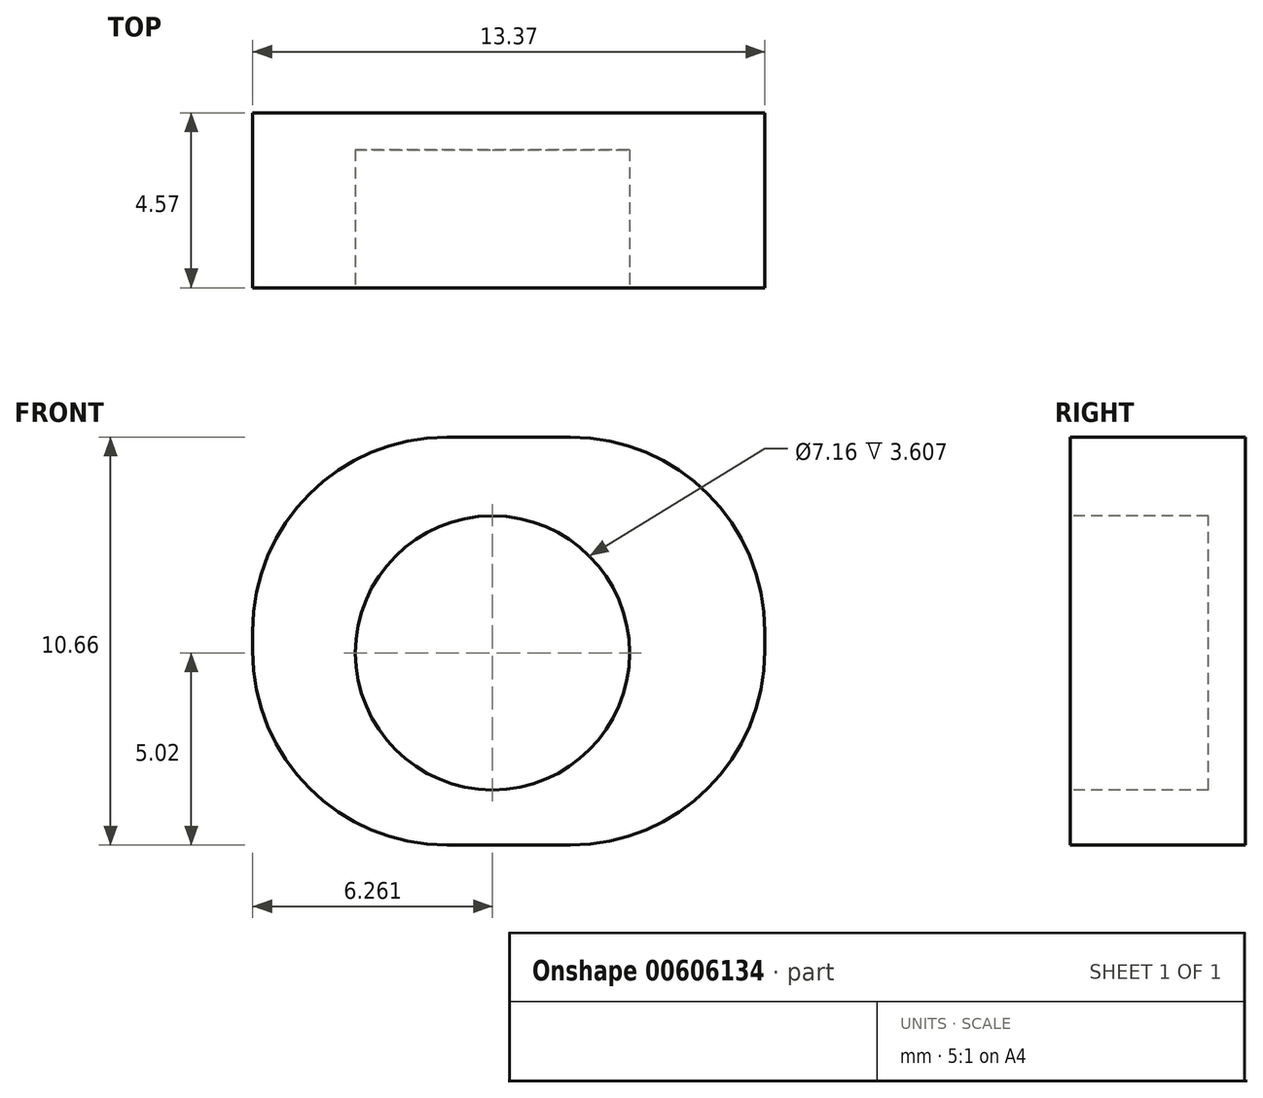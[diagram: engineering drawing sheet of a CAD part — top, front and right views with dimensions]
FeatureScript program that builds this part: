
annotation { "Feature Type Name" : "Feature", "Feature Type Description" : "" }
export const myFeature = defineFeature(function(context is Context, id is Id, definition is map)
    precondition{}
    {
        {
            var Q0;
            Q0=qCreatedBy(makeId("Front.planeOp"),FACE);
            var sketch = newSketch(context, id + "F0", { "sketchPlane" : qUnion([Q0])});
            skLineSegment(sketch, "E0.bottom", {"start": v(-10.53, -5.02) * mm, "end": v(2.84, -5.02) * mm});
            skLineSegment(sketch, "E0.top", {"start": v(-10.53, 5.64) * mm, "end": v(2.84, 5.64) * mm});
            skLineSegment(sketch, "E0.left", {"start": v(-10.53, -5.02) * mm, "end": v(-10.53, 5.64) * mm});
            skLineSegment(sketch, "E0.right", {"start": v(2.84, -5.02) * mm, "end": v(2.84, 5.64) * mm});
            skSolve(sketch);
        }
        {
            var Q0;
            Q0=qSketchRegion(id+"F0",true);
            extrude(context, id + "F1", {"entities" : qUnion([Q0]), "depth" : 4.57 * mm});
        }
        {
            var Q0;
            Q0=makeQuery(id+"F1.opExtrude","CAP_FACE",FACE,{"disambiguationData":[OSD([sQuery(id+"F0.wireOp",EDGE,"E0.bottom"),sQuery(id+"F0.wireOp",EDGE,"E0.top"),sQuery(id+"F0.wireOp",EDGE,"E0.left"),sQuery(id+"F0.wireOp",EDGE,"E0.right")])],"isStart":false});
            var sketch = newSketch(context, id + "F2", { "sketchPlane" : qUnion([Q0])});
            skCircle(sketch, "E1", {"center": v(-4.27, 0) * mm, "radius": 3.58 * mm});
            skSolve(sketch);
        }
        {
            var Q0;
            Q0=makeQuery(id+"F2.imprint","IMPRINT",FACE,{"disambiguationData":[TD([[makeQuery(id+"F2.imprint","IMPRINT",EDGE,{"derivedFrom":sQuery(id+"F2.wireOp",EDGE,"E1")}),1.0]])]});
            extrude(context, id + "F3", {"entities" : qUnion([Q0]), "operationType" : NewBodyOperationType.REMOVE, "oppositeDirection" : true, "depth" : 3.6 * mm});
        }
        {
            var Q0;
            Q0=makeQuery(id+"F1.opExtrude","SWEPT_EDGE",EDGE,{"disambiguationData":[OSD([sQuery(id+"F0.wireOp",EDGE,"E0.bottom"),sQuery(id+"F0.wireOp",EDGE,"E0.right")])]});
            var Q1;
            Q1=makeQuery(id+"F1.opExtrude","SWEPT_EDGE",EDGE,{"disambiguationData":[OSD([sQuery(id+"F0.wireOp",EDGE,"E0.top"),sQuery(id+"F0.wireOp",EDGE,"E0.right")])]});
            var Q2;
            Q2=makeQuery(id+"F1.opExtrude","SWEPT_EDGE",EDGE,{"disambiguationData":[OSD([sQuery(id+"F0.wireOp",EDGE,"E0.top"),sQuery(id+"F0.wireOp",EDGE,"E0.left")])]});
            var Q3;
            Q3=makeQuery(id+"F1.opExtrude","SWEPT_EDGE",EDGE,{"disambiguationData":[OSD([sQuery(id+"F0.wireOp",EDGE,"E0.bottom"),sQuery(id+"F0.wireOp",EDGE,"E0.left")])]});
            fillet(context, id + "F4", {"entities" : qUnion([Q0, Q1, Q2, Q3]), "radius" : 5.08 * mm, "tangentPropagation" : true, "allowEdgeOverflow" : false});
        }
    });
